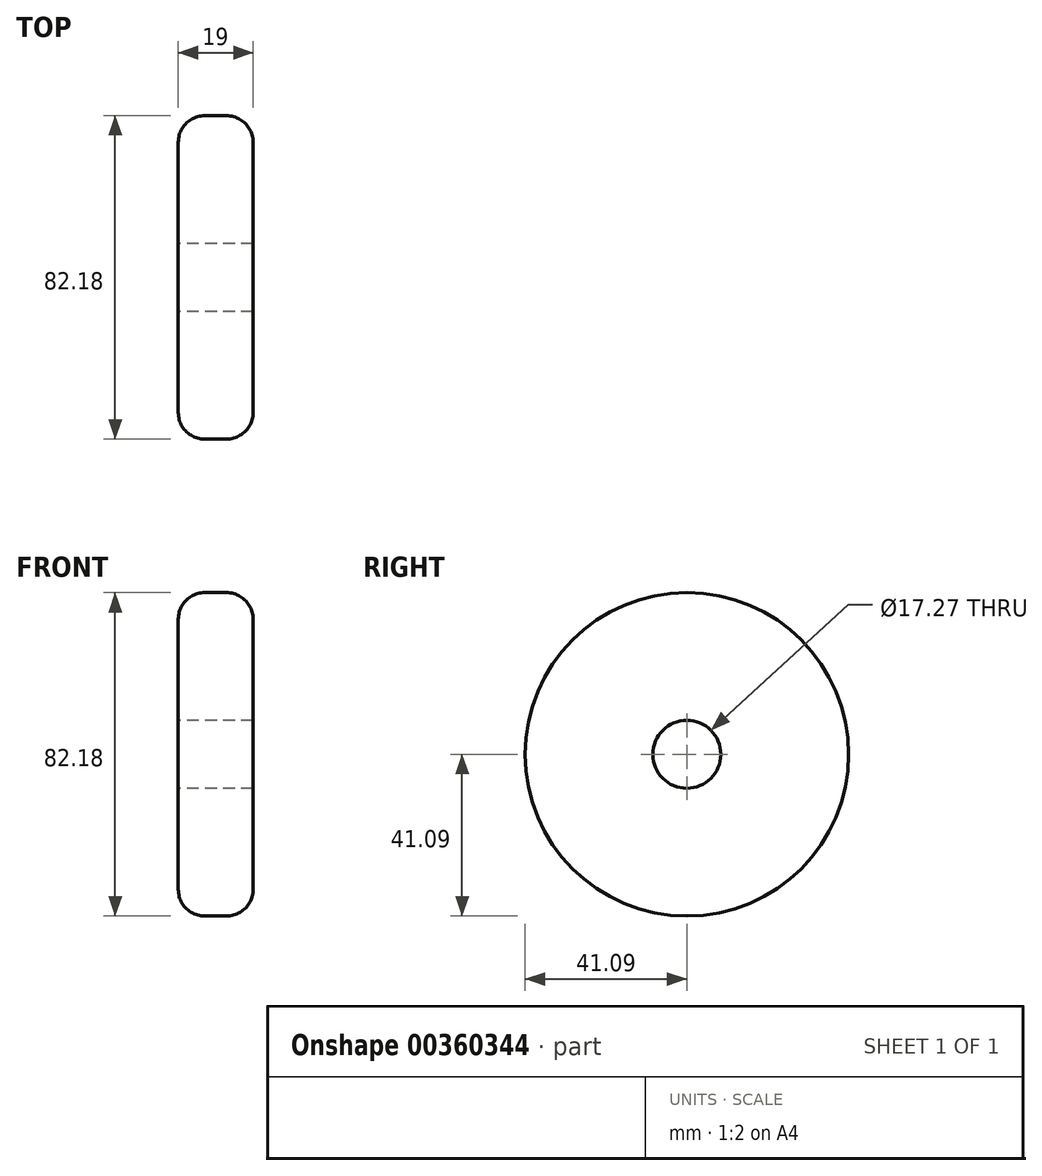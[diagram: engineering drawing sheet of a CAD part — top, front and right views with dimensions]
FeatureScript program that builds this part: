
annotation { "Feature Type Name" : "Feature", "Feature Type Description" : "" }
export const myFeature = defineFeature(function(context is Context, id is Id, definition is map)
    precondition{}
    {
        {
            var Q0;
            Q0=qCreatedBy(makeId("Right.planeOp"),FACE);
            var sketch = newSketch(context, id + "F0", { "sketchPlane" : qUnion([Q0])});
            skCircle(sketch, "E0", {"center": v(0, 0) * mm, "radius": 41.1 * mm});
            skSolve(sketch);
        }
        {
            var Q0;
            Q0=makeQuery(id+"F0.imprint","IMPRINT",FACE,{"disambiguationData":[TD([[makeQuery(id+"F0.imprint","IMPRINT",EDGE,{"derivedFrom":sQuery(id+"F0.wireOp",EDGE,"E0")}),1.0]])]});
            extrude(context, id + "F1", {"entities" : qUnion([Q0]), "depth" : 19 * mm});
        }
        {
            var Q0;
            Q0=makeQuery(id+"F1.opExtrude","CAP_EDGE",EDGE,{"disambiguationData":[OSD([sQuery(id+"F0.wireOp",EDGE,"E0")])],"isStart":false});
            var Q1;
            Q1=makeQuery(id+"F1.opExtrude","CAP_EDGE",EDGE,{"disambiguationData":[OSD([sQuery(id+"F0.wireOp",EDGE,"E0")])],"isStart":true});
            fillet(context, id + "F2", {"entities" : qUnion([Q0, Q1]), "radius" : 6.76 * mm, "tangentPropagation" : true, "allowEdgeOverflow" : false});
        }
        {
            var Q0;
            Q0=qCreatedBy(makeId("Right.planeOp"),FACE);
            var sketch = newSketch(context, id + "F3", { "sketchPlane" : qUnion([Q0])});
            skCircle(sketch, "E1", {"center": v(0, 0) * mm, "radius": 8.64 * mm});
            skSolve(sketch);
        }
        {
            var Q0;
            Q0 = qSketchRegion(id + "F3", true);
            extrude(context, id + "F4", {"entities" : qUnion([Q0]), "operationType" : NewBodyOperationType.REMOVE, "endBound" : BoundingType.SYMMETRIC, "depth" : 68.2 * mm});
        }
    });
